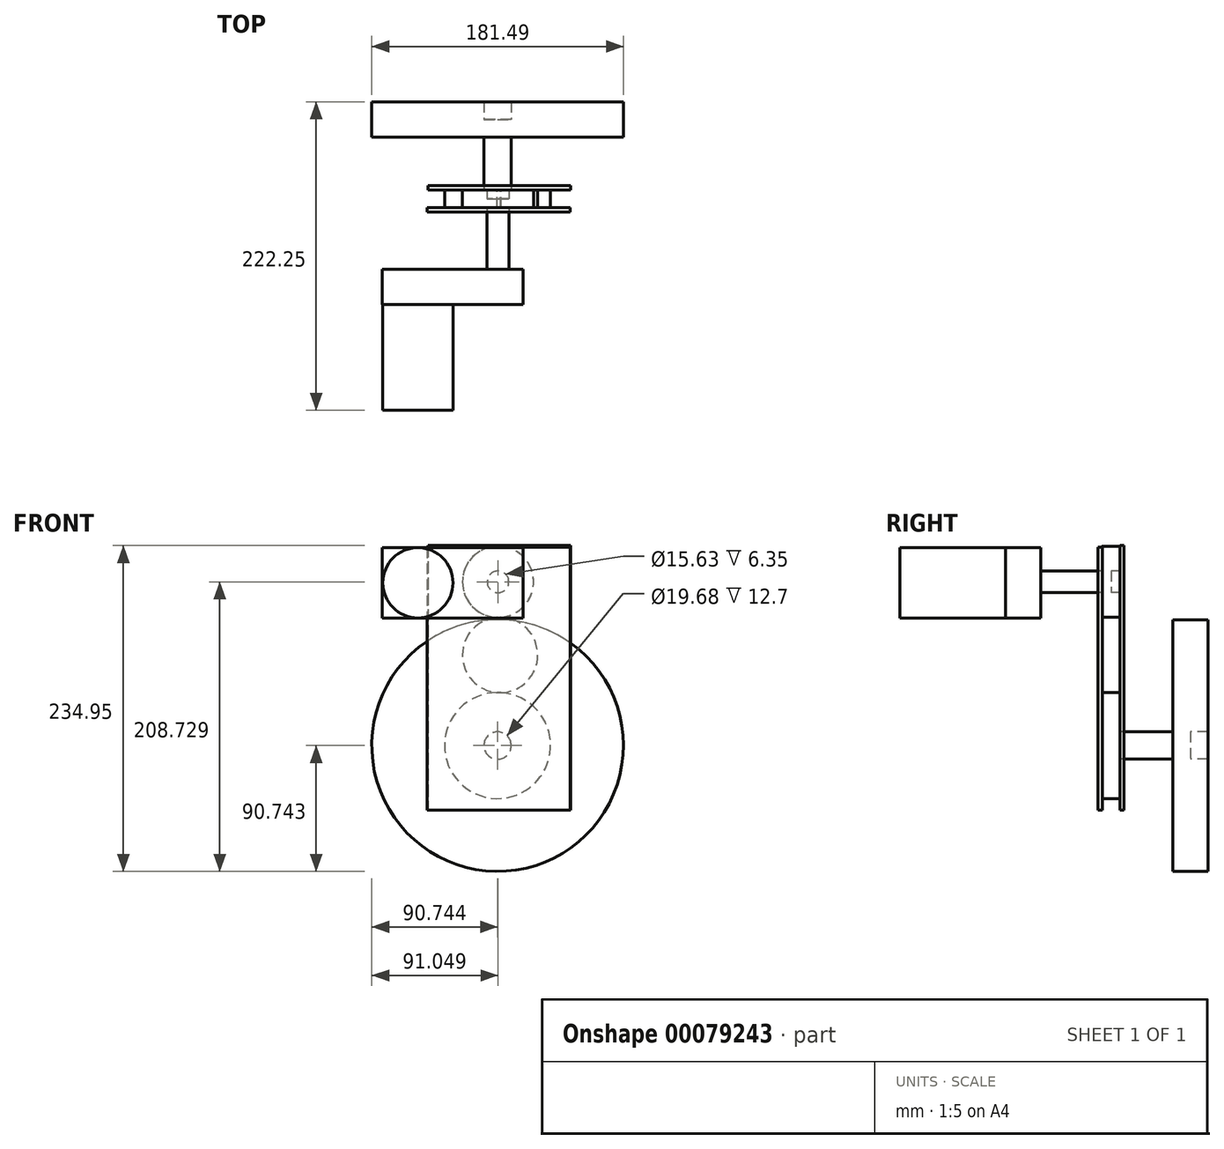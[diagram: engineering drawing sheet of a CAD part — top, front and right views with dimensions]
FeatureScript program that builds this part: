
annotation { "Feature Type Name" : "Feature", "Feature Type Description" : "" }
export const myFeature = defineFeature(function(context is Context, id is Id, definition is map)
    precondition{}
    {
        {
            var Q0;
            Q0=qCreatedBy(makeId("Front.planeOp"),FACE);
            var sketch = newSketch(context, id + "F0", { "sketchPlane" : qUnion([Q0])});
            skLineSegment(sketch, "E0.bottom", {"start": v(0, 0) * mm, "end": v(101.6, 0) * mm});
            skLineSegment(sketch, "E0.top", {"start": v(0, 50.8) * mm, "end": v(101.6, 50.8) * mm});
            skLineSegment(sketch, "E0.left", {"start": v(0, 0) * mm, "end": v(0, 50.8) * mm});
            skLineSegment(sketch, "E0.right", {"start": v(101.6, 0) * mm, "end": v(101.6, 50.8) * mm});
            skSolve(sketch);
        }
        {
            var Q0;
            Q0=makeQuery(id+"F0.imprint","IMPRINT",FACE,{"disambiguationData":[TD([[makeQuery(id+"F0.imprint","IMPRINT",EDGE,{"derivedFrom":sQuery(id+"F0.wireOp",EDGE,"E0.bottom")}),1.0]])]});
            extrude(context, id + "F1", {"entities" : qUnion([Q0]), "depth" : 25.4 * mm});
        }
        {
            var Q0;
            Q0=makeQuery(id+"F1.opExtrude","CAP_FACE",FACE,{"disambiguationData":[OSD([sQuery(id+"F0.wireOp",EDGE,"E0.bottom"),sQuery(id+"F0.wireOp",EDGE,"E0.top"),sQuery(id+"F0.wireOp",EDGE,"E0.left"),sQuery(id+"F0.wireOp",EDGE,"E0.right")])],"isStart":false});
            var sketch = newSketch(context, id + "F2", { "sketchPlane" : qUnion([Q0])});
            skCircle(sketch, "E1", {"center": v(25.68, 25.48) * mm, "radius": 25.32 * mm});
            skSolve(sketch);
        }
        {
            var Q0;
            Q0=makeQuery(id+"F2.imprint","IMPRINT",FACE,{"disambiguationData":[TD([[makeQuery(id+"F2.imprint","IMPRINT",EDGE,{"derivedFrom":sQuery(id+"F2.wireOp",EDGE,"E1")}),1.0]])]});
            extrude(context, id + "F3", {"entities" : qUnion([Q0]), "operationType" : NewBodyOperationType.ADD, "depth" : 76.2 * mm});
        }
        {
            var Q0;
            Q0=makeQuery(id+"F1.opExtrude","CAP_FACE",FACE,{"disambiguationData":[OSD([sQuery(id+"F0.wireOp",EDGE,"E0.bottom"),sQuery(id+"F0.wireOp",EDGE,"E0.top"),sQuery(id+"F0.wireOp",EDGE,"E0.left"),sQuery(id+"F0.wireOp",EDGE,"E0.right")])],"isStart":true});
            var sketch = newSketch(context, id + "F4", { "sketchPlane" : qUnion([Q0])});
            skCircle(sketch, "E2", {"center": v(-83.46, 26.13) * mm, "radius": 7.82 * mm});
            skSolve(sketch);
        }
        {
            var Q0;
            Q0=makeQuery(id+"F4.imprint","IMPRINT",FACE,{"disambiguationData":[TD([[makeQuery(id+"F4.imprint","IMPRINT",EDGE,{"derivedFrom":sQuery(id+"F4.wireOp",EDGE,"E2")}),1.0]])]});
            extrude(context, id + "F5", {"entities" : qUnion([Q0]), "operationType" : NewBodyOperationType.ADD, "depth" : 50.8 * mm});
        }
        {
            var Q0;
            Q0=makeQuery(id+"F5.opExtrude","CAP_FACE",FACE,{"disambiguationData":[OSD([sQuery(id+"F4.wireOp",EDGE,"E2")])],"isStart":false});
            var sketch = newSketch(context, id + "F6", { "sketchPlane" : qUnion([Q0])});
            skCircle(sketch, "E3", {"center": v(-83.46, 26.13) * mm, "radius": 25.64 * mm});
            skSolve(sketch);
        }
        {
            var Q0;
            Q0=makeQuery(id+"F6.imprint","IMPRINT",FACE,{"disambiguationData":[TD([[makeQuery(id+"F6.imprint","IMPRINT",EDGE,{"derivedFrom":sQuery(id+"F6.wireOp",EDGE,"E3")}),1.0]])]});
            extrude(context, id + "F7", {"entities" : qUnion([Q0]), "operationType" : NewBodyOperationType.ADD, "endBound" : BoundingType.SYMMETRIC, "depth" : 12.7 * mm});
        }
        {
            var Q0;
            Q0=makeQuery(id+"F7.opExtrude","CAP_FACE",FACE,{"disambiguationData":[OSD([sQuery(id+"F4.wireOp",EDGE,"E2"),sQuery(id+"F6.wireOp",EDGE,"E3")])],"isStart":false});
            var sketch = newSketch(context, id + "F8", { "sketchPlane" : qUnion([Q0])});
            skCircle(sketch, "E4", {"center": v(-84.95, -26.58) * mm, "radius": 27.15 * mm});
            skPoint(sketch, "E4.first.point", {"position": v(-85.5, 0.57) * mm});
            skPoint(sketch, "E4.second.point", {"position": v(-85.59, -53.72) * mm});
            skPoint(sketch, "E4.third.point", {"position": v(-80.72, -53.4) * mm});
            skCircle(sketch, "E5", {"center": v(-83.15, -91.86) * mm, "radius": 38.22 * mm});
            skPoint(sketch, "E5.second.point", {"position": v(-85.59, -130) * mm});
            skPoint(sketch, "E5.third.point", {"position": v(-80.72, -130) * mm});
            skSolve(sketch);
        }
        {
            var Q0;
            {var subQ0=sQuery(id+"F8.wireOp",EDGE,"E5");var subQ1=sQuery(id+"F8.wireOp",EDGE,"E4");var subQ2=makeQuery(id+"F8.imprint","INTERSECT",VERTEX,{"disambiguationData":[OD(0.0)],"derivedFrom":[subQ1,subQ0]});Q0=makeQuery(id+"F8.imprint","IMPRINT",FACE,{"disambiguationData":[TD([[makeQuery(id+"F8.imprint","IMPRINT",EDGE,{"disambiguationData":[TD([[subQ2,1.0]])],"derivedFrom":subQ1}),1.0]])]});}
            var Q1;
            {var subQ0=sQuery(id+"F8.wireOp",EDGE,"E5");var subQ1=sQuery(id+"F8.wireOp",EDGE,"E4");var subQ2=makeQuery(id+"F8.imprint","INTERSECT",VERTEX,{"disambiguationData":[OD(0.0)],"derivedFrom":[subQ1,subQ0]});Q1=makeQuery(id+"F8.imprint","IMPRINT",FACE,{"disambiguationData":[TD([[makeQuery(id+"F8.imprint","IMPRINT",EDGE,{"disambiguationData":[TD([[subQ2,-1.0]])],"derivedFrom":subQ1}),-1.0]])]});}
            extrude(context, id + "F9", {"entities" : qUnion([Q0, Q1]), "operationType" : NewBodyOperationType.ADD, "oppositeDirection" : true, "depth" : 12.7 * mm});
        }
        {
            var Q0;
            Q0=makeQuery(id+"F9.opExtrude","CAP_FACE",FACE,{"disambiguationData":[OSD([sQuery(id+"F8.wireOp",EDGE,"E4"),sQuery(id+"F8.wireOp",EDGE,"E5")])],"isStart":true});
            var sketch = newSketch(context, id + "F10", { "sketchPlane" : qUnion([Q0])});
            skCircle(sketch, "E6", {"center": v(-83.15, -91.86) * mm, "radius": 9.84 * mm});
            skSolve(sketch);
        }
        {
            var Q0;
            Q0=makeQuery(id+"F10.imprint","IMPRINT",FACE,{"disambiguationData":[TD([[makeQuery(id+"F10.imprint","IMPRINT",EDGE,{"derivedFrom":sQuery(id+"F10.wireOp",EDGE,"E6")}),1.0]])]});
            extrude(context, id + "F11", {"entities" : qUnion([Q0]), "operationType" : NewBodyOperationType.ADD, "depth" : 50.8 * mm});
        }
        {
            var Q0;
            Q0=makeQuery(id+"F11.opExtrude","CAP_FACE",FACE,{"disambiguationData":[OSD([sQuery(id+"F10.wireOp",EDGE,"E6")])],"isStart":false});
            var sketch = newSketch(context, id + "F12", { "sketchPlane" : qUnion([Q0])});
            skCircle(sketch, "E7", {"center": v(-83.15, -91.86) * mm, "radius": 90.74 * mm});
            skSolve(sketch);
        }
        {
            var Q0;
            Q0=makeQuery(id+"F12.imprint","IMPRINT",FACE,{"disambiguationData":[TD([[makeQuery(id+"F12.imprint","IMPRINT",EDGE,{"derivedFrom":sQuery(id+"F12.wireOp",EDGE,"E7")}),1.0]])]});
            extrude(context, id + "F13", {"entities" : qUnion([Q0]), "operationType" : NewBodyOperationType.ADD, "endBound" : BoundingType.SYMMETRIC, "depth" : 25.4 * mm});
        }
        {
            var Q0;
            {var subQ0=sQuery(id+"F6.wireOp",EDGE,"E3");Q0=makeQuery(id+"F9.boolean.opBoolean","MERGE",FACE,{"derivedFrom":[makeQuery(id+"F7.opExtrude","CAP_FACE",FACE,{"disambiguationData":[OSD([sQuery(id+"F4.wireOp",EDGE,"E2"),subQ0])],"isStart":false}),makeQuery(id+"F9.opExtrude","CAP_FACE",FACE,{"disambiguationData":[OSD([subQ0,sQuery(id+"F8.wireOp",EDGE,"E4"),sQuery(id+"F8.wireOp",EDGE,"E5")])],"isStart":true})]});}
            var sketch = newSketch(context, id + "F14", { "sketchPlane" : qUnion([Q0])});
            skLineSegment(sketch, "E8.bottom", {"start": v(-135.94, 52.35) * mm, "end": v(-32.86, 52.35) * mm});
            skLineSegment(sketch, "E8.top", {"start": v(-135.94, -138.36) * mm, "end": v(-32.86, -138.36) * mm});
            skLineSegment(sketch, "E8.left", {"start": v(-135.94, 52.35) * mm, "end": v(-135.94, -138.36) * mm});
            skLineSegment(sketch, "E8.right", {"start": v(-32.86, 52.35) * mm, "end": v(-32.86, -138.36) * mm});
            skSolve(sketch);
        }
        {
            var Q0;
            Q0=makeQuery(id+"F14.imprint","IMPRINT",FACE,{"disambiguationData":[TD([[makeQuery(id+"F14.imprint","IMPRINT",EDGE,{"derivedFrom":sQuery(id+"F14.wireOp",EDGE,"E8.bottom")}),-1.0]])]});
            var Q1;
            Q1=makeQuery(id+"F14.imprint","IMPRINT",FACE,{"disambiguationData":[TD([[makeQuery(id+"F14.imprint","IMPRINT",EDGE,{"derivedFrom":makeQuery(id+"F7.opExtrude","CAP_EDGE",EDGE,{"disambiguationData":[OSD([sQuery(id+"F4.wireOp",EDGE,"E2")])],"isStart":false})}),-1.0]])]});
            var Q2;
            Q2=makeQuery(id+"F14.imprint","IMPRINT",FACE,{"disambiguationData":[TD([[makeQuery(id+"F14.imprint","IMPRINT",EDGE,{"derivedFrom":makeQuery(id+"F7.opExtrude","CAP_EDGE",EDGE,{"disambiguationData":[OSD([sQuery(id+"F4.wireOp",EDGE,"E2")])],"isStart":false})}),1.0]])]});
            extrude(context, id + "F15", {"entities" : qUnion([Q0, Q1, Q2]), "depth" : 3.05 * mm});
        }
        {
            var Q0;
            Q0=makeQuery(id+"F9.opExtrude","CAP_FACE",FACE,{"disambiguationData":[OSD([sQuery(id+"F8.wireOp",EDGE,"E4"),sQuery(id+"F8.wireOp",EDGE,"E5")])],"isStart":false});
            var sketch = newSketch(context, id + "F16", { "sketchPlane" : qUnion([Q0])});
            skLineSegment(sketch, "E9.bottom", {"start": v(135.39, 51.25) * mm, "end": v(32.31, 51.25) * mm});
            skLineSegment(sketch, "E9.top", {"start": v(135.39, -138.36) * mm, "end": v(32.31, -138.36) * mm});
            skLineSegment(sketch, "E9.left", {"start": v(135.39, 51.25) * mm, "end": v(135.39, -138.36) * mm});
            skLineSegment(sketch, "E9.right", {"start": v(32.31, 51.25) * mm, "end": v(32.31, -138.36) * mm});
            skSolve(sketch);
        }
        {
            var Q0;
            Q0=makeQuery(id+"F16.imprint","IMPRINT",FACE,{"disambiguationData":[TD([[makeQuery(id+"F16.imprint","IMPRINT",EDGE,{"derivedFrom":sQuery(id+"F16.wireOp",EDGE,"E9.bottom")}),1.0]])]});
            var Q1;
            {var subQ0=sQuery(id+"F8.wireOp",EDGE,"E5");var subQ1=sQuery(id+"F8.wireOp",EDGE,"E4");var subQ2=makeQuery(id+"F8.imprint","INTERSECT",VERTEX,{"disambiguationData":[OD(0.0)],"derivedFrom":[subQ1,subQ0]});Q1=makeQuery(id+"F16.imprint","IMPRINT",FACE,{"disambiguationData":[TD([[makeQuery(id+"F16.imprint","IMPRINT",EDGE,{"derivedFrom":makeQuery(id+"F9.opExtrude","CAP_EDGE",EDGE,{"disambiguationData":[OSD([subQ1]),TDD([makeQuery(id+"F8.imprint","IMPRINT",EDGE,{"disambiguationData":[TD([[subQ2,-1.0]])],"derivedFrom":subQ1})])],"isStart":false})}),1.0]])]});}
            extrude(context, id + "F17", {"entities" : qUnion([Q0, Q1]), "depth" : 3.05 * mm});
        }
    });
